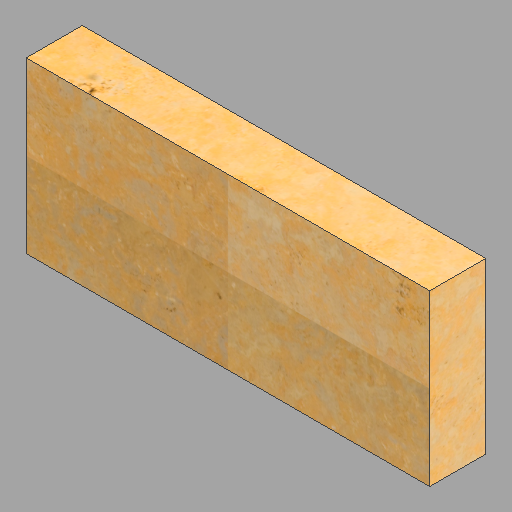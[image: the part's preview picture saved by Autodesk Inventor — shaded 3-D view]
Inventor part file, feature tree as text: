
AUTODESK INVENTOR PART (.ipt)
format: ipt  version: 2023 (Build 270158030, 158C)  size: 354,816 bytes
history: native  units: in
note: dims shown in document units (in); Inventor stores cm internally (conversion verified against a paired STEP export)
features: extrude x1, sketch x1
ambient origin geometry x8: Origin, YZ Plane, XZ Plane, XY Plane, X Axis, Y Axis, Z Axis, Center Point
bodies: Solid1 (feature_tree)
feature tree (2):
  extrude  "Extrusion1"  Depth=15.125in
  sketch  "Sketch1"  dims[d0=36.0in d1=15.125in d2=5.0in d3=0.0in]
